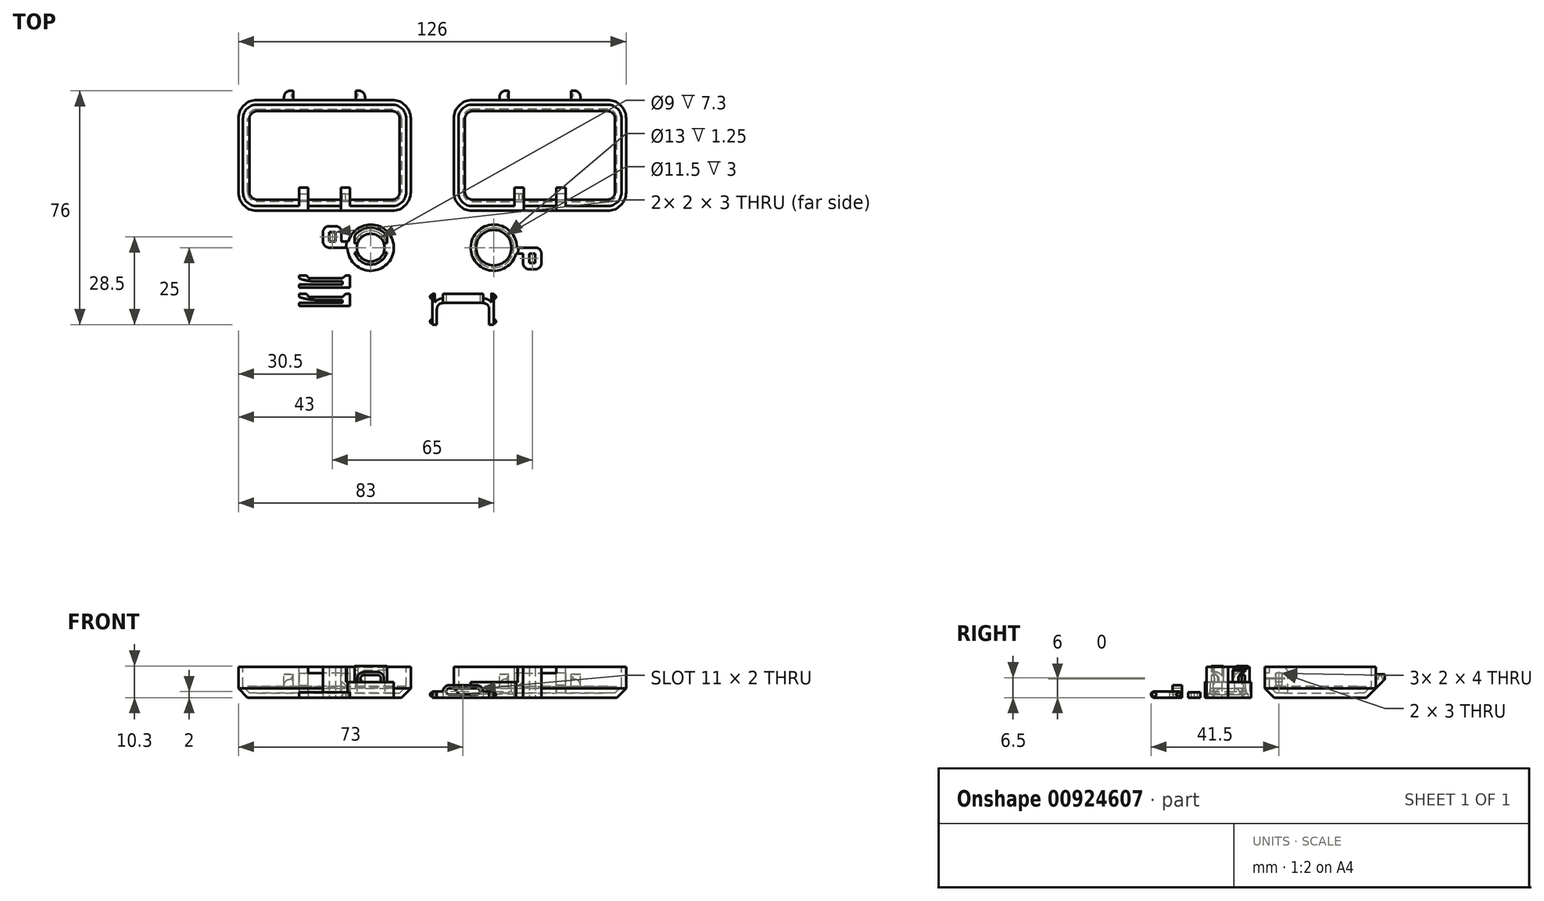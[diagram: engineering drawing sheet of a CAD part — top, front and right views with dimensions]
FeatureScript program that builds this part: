
annotation { "Feature Type Name" : "Feature", "Feature Type Description" : "" }
export const myFeature = defineFeature(function(context is Context, id is Id, definition is map)
    precondition{}
    {
        {
            var Q0;
            Q0=qCreatedBy(makeId("Top.planeOp"),FACE);
            var sketch = newSketch(context, id + "F0", { "sketchPlane" : qUnion([Q0])});
            skCircle(sketch, "E0", {"center": v(-20, 0) * mm, "radius": 7.5 * mm});
            skLineSegment(sketch, "E1", {"start": v(0, 7) * mm, "end": v(0, 0) * mm, "construction": true});
            skLineSegment(sketch, "E2", {"start": v(-27.5, 0) * mm, "end": v(-33.5, 0) * mm});
            skLineSegment(sketch, "E3", {"start": v(-35.5, 2) * mm, "end": v(-35.5, 5) * mm});
            skLineSegment(sketch, "E4", {"start": v(-33.5, 7) * mm, "end": v(-31.5, 7) * mm});
            skLineSegment(sketch, "E5", {"start": v(-29.5, 5) * mm, "end": v(-29.5, 2) * mm});
            skLineSegment(sketch, "E6", {"start": v(-29.5, 2) * mm, "end": v(-27.23, 2) * mm});
            skLineSegment(sketch, "E7.bottom", {"start": v(-33.5, 5) * mm, "end": v(-31.5, 5) * mm});
            skLineSegment(sketch, "E7.top", {"start": v(-33.5, 2) * mm, "end": v(-31.5, 2) * mm});
            skLineSegment(sketch, "E7.left", {"start": v(-33.5, 5) * mm, "end": v(-33.5, 2) * mm});
            skLineSegment(sketch, "E7.right", {"start": v(-31.5, 5) * mm, "end": v(-31.5, 2) * mm});
            skCircle(sketch, "E8", {"center": v(-20, 0) * mm, "radius": 4.5 * mm});
            skPoint(sketch, "E9.visualSharp", {"position": v(-35.5, 0) * mm});
            skArc(sketch, "E9.filletArc", {"start": v(-35.5, 2) * mm, "mid": v(-34.91, 0.59) * mm, "end": v(-33.5, 0) * mm});
            skPoint(sketch, "E10.visualSharp", {"position": v(-35.5, 7) * mm});
            skArc(sketch, "E10.filletArc", {"start": v(-33.5, 7) * mm, "mid": v(-34.91, 6.41) * mm, "end": v(-35.5, 5) * mm});
            skPoint(sketch, "E11.visualSharp", {"position": v(-29.5, 7) * mm});
            skArc(sketch, "E11.filletArc", {"start": v(-29.5, 5) * mm, "mid": v(-30.09, 6.41) * mm, "end": v(-31.5, 7) * mm});
            skCircle(sketch, "E12.MirrorC", {"center": v(20, 0) * mm, "radius": 7.5 * mm});
            skLineSegment(sketch, "E13.MirrorCS", {"start": v(27.5, 0) * mm, "end": v(33.5, 0) * mm});
            skLineSegment(sketch, "E14.MirrorCS", {"start": v(29.5, 2) * mm, "end": v(27.23, 2) * mm, "construction": true});
            skLineSegment(sketch, "E15.MirrorCS", {"start": v(29.5, 5) * mm, "end": v(29.5, 2) * mm, "construction": true});
            skArc(sketch, "E16.MirrorCS", {"start": v(29.5, 5) * mm, "mid": v(30.09, 6.41) * mm, "end": v(31.5, 7) * mm, "construction": true});
            skLineSegment(sketch, "E17.MirrorCS", {"start": v(33.5, 7) * mm, "end": v(31.5, 7) * mm, "construction": true});
            skArc(sketch, "E18.MirrorCS", {"start": v(33.5, 7) * mm, "mid": v(34.91, 6.41) * mm, "end": v(35.5, 5) * mm, "construction": true});
            skLineSegment(sketch, "E19.MirrorCS", {"start": v(35.5, 2) * mm, "end": v(35.5, 5) * mm, "construction": true});
            skArc(sketch, "E20.MirrorCS", {"start": v(35.5, 2) * mm, "mid": v(34.91, 0.59) * mm, "end": v(33.5, 0) * mm, "construction": true});
            skLineSegment(sketch, "E21.MirrorCS", {"start": v(33.5, 5) * mm, "end": v(33.5, 2) * mm, "construction": true});
            skLineSegment(sketch, "E22.MirrorCS", {"start": v(33.5, 5) * mm, "end": v(31.5, 5) * mm, "construction": true});
            skLineSegment(sketch, "E23.MirrorCS", {"start": v(31.5, 5) * mm, "end": v(31.5, 2) * mm, "construction": true});
            skLineSegment(sketch, "E24.MirrorCS", {"start": v(33.5, 2) * mm, "end": v(31.5, 2) * mm, "construction": true});
            skCircle(sketch, "E25", {"center": v(20, 0) * mm, "radius": 6.5 * mm});
            skLineSegment(sketch, "E26.MirrorCS", {"start": v(29.5, -2) * mm, "end": v(27.23, -2) * mm});
            skLineSegment(sketch, "E27.MirrorCS", {"start": v(29.5, -5) * mm, "end": v(29.5, -2) * mm});
            skArc(sketch, "E28.MirrorCS", {"start": v(29.5, -5) * mm, "mid": v(30.09, -6.41) * mm, "end": v(31.5, -7) * mm});
            skLineSegment(sketch, "E29.MirrorCS", {"start": v(33.5, -7) * mm, "end": v(31.5, -7) * mm});
            skArc(sketch, "E30.MirrorCS", {"start": v(33.5, -7) * mm, "mid": v(34.91, -6.41) * mm, "end": v(35.5, -5) * mm});
            skLineSegment(sketch, "E31.MirrorCS", {"start": v(35.5, -2) * mm, "end": v(35.5, -5) * mm});
            skArc(sketch, "E32.MirrorCS", {"start": v(35.5, -2) * mm, "mid": v(34.91, -0.59) * mm, "end": v(33.5, 0) * mm});
            skLineSegment(sketch, "E33.MirrorCS", {"start": v(33.5, -5) * mm, "end": v(33.5, -2) * mm});
            skLineSegment(sketch, "E34.MirrorCS", {"start": v(33.5, -2) * mm, "end": v(31.5, -2) * mm});
            skLineSegment(sketch, "E35.MirrorCS", {"start": v(31.5, -5) * mm, "end": v(31.5, -2) * mm});
            skLineSegment(sketch, "E36.MirrorCS", {"start": v(33.5, -5) * mm, "end": v(31.5, -5) * mm});
            skSolve(sketch);
        }
        {
            var Q0;
            Q0=makeQuery(id+"F0.imprint","IMPRINT",FACE,{"disambiguationData":[TD([[makeQuery(id+"F0.imprint","IMPRINT",EDGE,{"derivedFrom":sQuery(id+"F0.wireOp",EDGE,"E8")}),-1.0]])]});
            var Q1;
            Q1=makeQuery(id+"F0.imprint","IMPRINT",FACE,{"disambiguationData":[TD([[makeQuery(id+"F0.imprint","IMPRINT",EDGE,{"derivedFrom":sQuery(id+"F0.wireOp",EDGE,"E25")}),-1.0]])]});
            extrude(context, id + "F1", {"entities" : qUnion([Q0, Q1]), "depth" : 5 * mm, "offsetDistance" : 25 * mm});
        }
        {
            var Q0;
            Q0=makeQuery(id+"F1.opExtrude","CAP_FACE",FACE,{"disambiguationData":[OSD([sQuery(id+"F0.wireOp",EDGE,"E0"),sQuery(id+"F0.wireOp",EDGE,"E2"),sQuery(id+"F0.wireOp",EDGE,"E3"),sQuery(id+"F0.wireOp",EDGE,"E4"),sQuery(id+"F0.wireOp",EDGE,"E5"),sQuery(id+"F0.wireOp",EDGE,"E6"),sQuery(id+"F0.wireOp",EDGE,"E7.bottom"),sQuery(id+"F0.wireOp",EDGE,"E7.top"),sQuery(id+"F0.wireOp",EDGE,"E7.left"),sQuery(id+"F0.wireOp",EDGE,"E7.right"),sQuery(id+"F0.wireOp",EDGE,"E8"),sQuery(id+"F0.wireOp",EDGE,"E9.filletArc"),sQuery(id+"F0.wireOp",EDGE,"E10.filletArc"),sQuery(id+"F0.wireOp",EDGE,"E11.filletArc")])],"isStart":false});
            var sketch = newSketch(context, id + "F2", { "sketchPlane" : qUnion([Q0])});
            skArc(sketch, "E37.0", {"start": v(-24.24, -1.5) * mm, "mid": v(-20, -4.5) * mm, "end": v(-15.76, -1.5) * mm});
            skArc(sketch, "E38", {"start": v(-25.3, -1.5) * mm, "mid": v(-20, -5.5) * mm, "end": v(-14.7, -1.5) * mm});
            skLineSegment(sketch, "E39.0", {"start": v(0, 7) * mm, "end": v(0, 0) * mm, "construction": true});
            skLineSegment(sketch, "E40.bottom", {"start": v(-10, -1.5) * mm, "end": v(-14.7, -1.5) * mm, "construction": true});
            skLineSegment(sketch, "E40.top", {"start": v(-10, 1.5) * mm, "end": v(-14.7, 1.5) * mm, "construction": true});
            skLineSegment(sketch, "E40.left", {"start": v(-10, -1.5) * mm, "end": v(-10, 1.5) * mm, "construction": true});
            skLineSegment(sketch, "E40.right", {"start": v(-30, -1.5) * mm, "end": v(-30, 1.5) * mm, "construction": true});
            skArc(sketch, "E41.trimOffspring", {"start": v(-15.76, 1.5) * mm, "mid": v(-20, 4.5) * mm, "end": v(-24.24, 1.5) * mm});
            skArc(sketch, "E42.trimOffspring", {"start": v(-14.7, 1.5) * mm, "mid": v(-20, 5.5) * mm, "end": v(-25.3, 1.5) * mm});
            skLineSegment(sketch, "E43", {"start": v(-25.3, 1.5) * mm, "end": v(-30, 1.5) * mm, "construction": true});
            skLineSegment(sketch, "E44", {"start": v(-24.24, 1.5) * mm, "end": v(-25.3, 1.5) * mm});
            skLineSegment(sketch, "E45", {"start": v(-24.24, -1.5) * mm, "end": v(-25.3, -1.5) * mm});
            skLineSegment(sketch, "E46", {"start": v(-25.3, -1.5) * mm, "end": v(-30, -1.5) * mm, "construction": true});
            skLineSegment(sketch, "E47", {"start": v(-15.76, -1.5) * mm, "end": v(-24.24, -1.5) * mm, "construction": true});
            skLineSegment(sketch, "E48", {"start": v(-14.7, -1.5) * mm, "end": v(-15.76, -1.5) * mm});
            skLineSegment(sketch, "E49", {"start": v(-15.76, 1.5) * mm, "end": v(-24.24, 1.5) * mm, "construction": true});
            skLineSegment(sketch, "E50", {"start": v(-14.7, 1.5) * mm, "end": v(-15.76, 1.5) * mm});
            skCircle(sketch, "E51.0", {"center": v(20, 0) * mm, "radius": 6.5 * mm});
            skCircle(sketch, "E52", {"center": v(20, 0) * mm, "radius": 5.75 * mm});
            skCircle(sketch, "E53", {"center": v(-20, 0) * mm, "radius": 8 * mm});
            skCircle(sketch, "E54.0", {"center": v(-20, 0) * mm, "radius": 7.5 * mm, "construction": true});
            skCircle(sketch, "E55.MirrorC", {"center": v(20, 0) * mm, "radius": 8 * mm});
            skSolve(sketch);
        }
        {
            var Q0;
            Q0=makeQuery(id+"F2.imprint","IMPRINT",FACE,{"disambiguationData":[TD([[makeQuery(id+"F2.imprint","IMPRINT",EDGE,{"derivedFrom":sQuery(id+"F2.wireOp",EDGE,"E37.0")}),-1.0]])]});
            var Q1;
            Q1=makeQuery(id+"F2.imprint","IMPRINT",FACE,{"disambiguationData":[TD([[makeQuery(id+"F2.imprint","IMPRINT",EDGE,{"derivedFrom":sQuery(id+"F2.wireOp",EDGE,"E41.trimOffspring")}),-1.0]])]});
            extrude(context, id + "F3", {"entities" : qUnion([Q0, Q1]), "operationType" : NewBodyOperationType.ADD, "depth" : 5.3 * mm, "offsetDistance" : 25 * mm});
        }
        {
            var Q0;
            Q0=makeQuery(id+"F2.imprint","IMPRINT",FACE,{"disambiguationData":[TD([[makeQuery(id+"F2.imprint","IMPRINT",EDGE,{"derivedFrom":sQuery(id+"F2.wireOp",EDGE,"E51.0")}),1.0]])]});
            extrude(context, id + "F4", {"entities" : qUnion([Q0]), "operationType" : NewBodyOperationType.ADD, "oppositeDirection" : true, "depth" : 4 * mm, "offsetDistance" : 25 * mm});
        }
        {
            var Q0;
            {var subQ1=sQuery(id+"F0.wireOp",EDGE,"E2");Q0=makeQuery(id+"F0.imprint","IMPRINT",FACE,{"disambiguationData":[TD([[makeQuery(id+"F0.imprint","IMPRINT",EDGE,{"derivedFrom":subQ1}),-1.0]])]});}
            var Q1;
            {var subQ0=sQuery(id+"F0.wireOp",EDGE,"E13.MirrorCS");Q1=makeQuery(id+"F0.imprint","IMPRINT",FACE,{"disambiguationData":[TD([[makeQuery(id+"F0.imprint","IMPRINT",EDGE,{"derivedFrom":subQ0}),1.0]])]});}
            var Q2;
            {var subQ0=sQuery(id+"F0.wireOp",EDGE,"E13.MirrorCS");Q2=makeQuery(id+"F0.imprint","IMPRINT",FACE,{"disambiguationData":[TD([[makeQuery(id+"F0.imprint","IMPRINT",EDGE,{"derivedFrom":subQ0}),-1.0]])]});}
            extrude(context, id + "F5", {"entities" : qUnion([Q0, Q1, Q2]), "operationType" : NewBodyOperationType.ADD, "depth" : 10 * mm, "offsetDistance" : 25 * mm});
        }
        {
            var Q0;
            Q0=makeQuery(id+"F3.opExtrude","CAP_FACE",FACE,{"disambiguationData":[OSD([sQuery(id+"F2.wireOp",EDGE,"E41.trimOffspring"),sQuery(id+"F2.wireOp",EDGE,"E42.trimOffspring"),sQuery(id+"F2.wireOp",EDGE,"E44"),sQuery(id+"F2.wireOp",EDGE,"E50")])],"isStart":false});
            var sketch = newSketch(context, id + "F6", { "sketchPlane" : qUnion([Q0])});
            skArc(sketch, "E56.0", {"start": v(-14.7, 1.5) * mm, "mid": v(-20, 5.5) * mm, "end": v(-25.3, 1.5) * mm});
            skArc(sketch, "E57.0", {"start": v(-13.68, 1.5) * mm, "mid": v(-20, 6.5) * mm, "end": v(-26.32, 1.5) * mm});
            skLineSegment(sketch, "E58", {"start": v(-25.3, 1.5) * mm, "end": v(-26.32, 1.5) * mm});
            skLineSegment(sketch, "E59", {"start": v(-14.7, 1.5) * mm, "end": v(-13.68, 1.5) * mm});
            skLineSegment(sketch, "E60", {"start": v(-20, 0) * mm, "end": v(0, 0) * mm, "construction": true});
            skArc(sketch, "E61.MirrorCS", {"start": v(-14.7, -1.5) * mm, "mid": v(-20, -5.5) * mm, "end": v(-25.3, -1.5) * mm});
            skArc(sketch, "E62.MirrorCS", {"start": v(-13.68, -1.5) * mm, "mid": v(-20, -6.5) * mm, "end": v(-26.32, -1.5) * mm});
            skLineSegment(sketch, "E63.MirrorCS", {"start": v(-25.3, -1.5) * mm, "end": v(-26.32, -1.5) * mm});
            skLineSegment(sketch, "E64.MirrorCS", {"start": v(-14.7, -1.5) * mm, "end": v(-13.68, -1.5) * mm});
            skSolve(sketch);
        }
        {
            var Q0;
            Q0=makeQuery(id+"F6.imprint","IMPRINT",FACE,{"disambiguationData":[TD([[makeQuery(id+"F6.imprint","IMPRINT",EDGE,{"derivedFrom":sQuery(id+"F6.wireOp",EDGE,"E61.MirrorCS")}),1.0]])]});
            var Q1;
            Q1=makeQuery(id+"F6.imprint","IMPRINT",FACE,{"disambiguationData":[TD([[makeQuery(id+"F6.imprint","IMPRINT",EDGE,{"derivedFrom":sQuery(id+"F6.wireOp",EDGE,"E56.0")}),-1.0]])]});
            extrude(context, id + "F7", {"entities" : qUnion([Q0, Q1]), "operationType" : NewBodyOperationType.ADD, "oppositeDirection" : true, "depth" : 1.5 * mm, "offsetDistance" : 25 * mm});
        }
        {
            var Q0;
            Q0=makeQuery(id+"F4.opExtrude","CAP_EDGE",EDGE,{"disambiguationData":[OSD([sQuery(id+"F2.wireOp",EDGE,"E52")])],"isStart":false});
            var Q1;
            Q1=makeQuery(id+"F7.opExtrude","CAP_EDGE",EDGE,{"disambiguationData":[OSD([sQuery(id+"F6.wireOp",EDGE,"E62.MirrorCS")])],"isStart":false});
            var Q2;
            Q2=makeQuery(id+"F7.opExtrude","CAP_EDGE",EDGE,{"disambiguationData":[OSD([sQuery(id+"F6.wireOp",EDGE,"E57.0")])],"isStart":false});
            chamfer(context, id + "F8", {"entities" : qUnion([Q0, Q1, Q2]), "width" : 1 * mm, "tangentPropagation" : true});
        }
        {
            var Q0;
            Q0=makeQuery(id+"F2.imprint","IMPRINT",FACE,{"disambiguationData":[TD([[makeQuery(id+"F2.imprint","IMPRINT",EDGE,{"derivedFrom":sQuery(id+"F2.wireOp",EDGE,"E53")}),1.0]])]});
            var Q1;
            Q1=makeQuery(id+"F2.imprint","IMPRINT",FACE,{"disambiguationData":[TD([[makeQuery(id+"F2.imprint","IMPRINT",EDGE,{"derivedFrom":sQuery(id+"F2.wireOp",EDGE,"E51.0")}),-1.0]])]});
            extrude(context, id + "F9", {"entities" : qUnion([Q0, Q1]), "operationType" : NewBodyOperationType.REMOVE, "endBound" : BoundingType.THROUGH_ALL, "depth" : 25 * mm, "offsetDistance" : 25 * mm});
        }
        {
            var Q0;
            Q0=qCreatedBy(makeId("Front.planeOp"),FACE);
            var sketch = newSketch(context, id + "F10", { "sketchPlane" : qUnion([Q0])});
            skLineSegment(sketch, "E65.0.0", {"start": v(-25.3, 5) * mm, "end": v(-14.7, 5) * mm, "construction": true});
            skLineSegment(sketch, "E65.0.1", {"start": v(-14.7, 5) * mm, "end": v(-14.7, 8.8) * mm, "construction": true});
            skLineSegment(sketch, "E65.0.2", {"start": v(-14.7, 8.8) * mm, "end": v(-25.3, 8.8) * mm, "construction": true});
            skLineSegment(sketch, "E65.0.3", {"start": v(-25.3, 8.8) * mm, "end": v(-25.3, 5) * mm, "construction": true});
            skLineSegment(sketch, "E66.bottom", {"start": v(-24.3, 5) * mm, "end": v(-15.7, 5) * mm});
            skLineSegment(sketch, "E66.top", {"start": v(-22.3, 8.3) * mm, "end": v(-17.7, 8.3) * mm});
            skLineSegment(sketch, "E66.left", {"start": v(-24.3, 5) * mm, "end": v(-24.3, 6.3) * mm});
            skLineSegment(sketch, "E66.right", {"start": v(-15.7, 5) * mm, "end": v(-15.7, 6.3) * mm});
            skLineSegment(sketch, "E67.bottom", {"start": v(-23.3, 5) * mm, "end": v(-16.7, 5) * mm});
            skLineSegment(sketch, "E67.top", {"start": v(-22.3, 7.3) * mm, "end": v(-17.7, 7.3) * mm});
            skLineSegment(sketch, "E67.left", {"start": v(-23.3, 5) * mm, "end": v(-23.3, 6.3) * mm});
            skLineSegment(sketch, "E67.right", {"start": v(-16.7, 5) * mm, "end": v(-16.7, 6.3) * mm});
            skPoint(sketch, "E68.visualSharp", {"position": v(-23.3, 7.3) * mm});
            skArc(sketch, "E68.filletArc", {"start": v(-22.3, 7.3) * mm, "mid": v(-23, 7) * mm, "end": v(-23.3, 6.3) * mm});
            skPoint(sketch, "E69.visualSharp", {"position": v(-16.7, 7.3) * mm});
            skArc(sketch, "E69.filletArc", {"start": v(-16.7, 6.3) * mm, "mid": v(-17, 7) * mm, "end": v(-17.7, 7.3) * mm});
            skPoint(sketch, "E70.visualSharp", {"position": v(-15.7, 8.3) * mm});
            skArc(sketch, "E70.filletArc", {"start": v(-15.7, 6.3) * mm, "mid": v(-16.3, 7.71) * mm, "end": v(-17.7, 8.3) * mm});
            skPoint(sketch, "E71.visualSharp", {"position": v(-24.3, 8.3) * mm});
            skArc(sketch, "E71.filletArc", {"start": v(-22.3, 8.3) * mm, "mid": v(-23.7, 7.71) * mm, "end": v(-24.3, 6.3) * mm});
            skLineSegment(sketch, "E72.bottom", {"start": v(-25.3, 5) * mm, "end": v(-27.3, 5) * mm});
            skLineSegment(sketch, "E72.top", {"start": v(-25.3, 11) * mm, "end": v(-27.3, 11) * mm});
            skLineSegment(sketch, "E72.left", {"start": v(-25.3, 5) * mm, "end": v(-25.3, 11) * mm});
            skLineSegment(sketch, "E72.right", {"start": v(-27.3, 5) * mm, "end": v(-27.3, 11) * mm});
            skLineSegment(sketch, "E73.bottom", {"start": v(-14.7, 5) * mm, "end": v(-12.7, 5) * mm});
            skLineSegment(sketch, "E73.top", {"start": v(-14.7, 11) * mm, "end": v(-12.7, 11) * mm});
            skLineSegment(sketch, "E73.left", {"start": v(-14.7, 5) * mm, "end": v(-14.7, 11) * mm});
            skLineSegment(sketch, "E73.right", {"start": v(-12.7, 5) * mm, "end": v(-12.7, 11) * mm});
            skSolve(sketch);
        }
        {
            var Q0;
            Q0=makeQuery(id+"F10.imprint","IMPRINT",FACE,{"disambiguationData":[TD([[makeQuery(id+"F10.imprint","IMPRINT",EDGE,{"derivedFrom":sQuery(id+"F10.wireOp",EDGE,"E66.top")}),-1.0]])]});
            var Q1;
            Q1=makeQuery(id+"F10.imprint","IMPRINT",FACE,{"disambiguationData":[TD([[makeQuery(id+"F10.imprint","IMPRINT",EDGE,{"derivedFrom":sQuery(id+"F10.wireOp",EDGE,"E72.bottom")}),-1.0]])]});
            var Q2;
            Q2=makeQuery(id+"F10.imprint","IMPRINT",FACE,{"disambiguationData":[TD([[makeQuery(id+"F10.imprint","IMPRINT",EDGE,{"derivedFrom":sQuery(id+"F10.wireOp",EDGE,"E73.bottom")}),1.0]])]});
            extrude(context, id + "F11", {"entities" : qUnion([Q0, Q1, Q2]), "operationType" : NewBodyOperationType.REMOVE, "endBound" : BoundingType.THROUGH_ALL, "oppositeDirection" : true, "depth" : 25 * mm, "offsetDistance" : 25 * mm, "hasSecondDirection" : true, "secondDirectionBound" : SecondDirectionBoundingType.THROUGH_ALL, "secondDirectionOppositeDirection" : false, "secondDirectionDepth" : 25 * mm});
        }
        {
            var Q0;
            Q0=qCreatedBy(makeId("Top.planeOp"),FACE);
            var sketch = newSketch(context, id + "F12", { "sketchPlane" : qUnion([Q0])});
            skLineSegment(sketch, "E74.bottom", {"start": v(-13, 15) * mm, "end": v(-57, 15) * mm});
            skLineSegment(sketch, "E74.top", {"start": v(-13, 45) * mm, "end": v(-57, 45) * mm});
            skLineSegment(sketch, "E74.left", {"start": v(-10, 18) * mm, "end": v(-10, 42) * mm});
            skLineSegment(sketch, "E74.right", {"start": v(-60, 18) * mm, "end": v(-60, 42) * mm});
            skPoint(sketch, "E74.middle", {"position": v(-35, 30) * mm});
            skPoint(sketch, "E75.visualSharp", {"position": v(-60, 45) * mm});
            skArc(sketch, "E75.filletArc", {"start": v(-57, 45) * mm, "mid": v(-59.12, 44.12) * mm, "end": v(-60, 42) * mm});
            skPoint(sketch, "E76.visualSharp", {"position": v(-10, 45) * mm});
            skArc(sketch, "E76.filletArc", {"start": v(-10, 42) * mm, "mid": v(-10.88, 44.12) * mm, "end": v(-13, 45) * mm});
            skPoint(sketch, "E77.visualSharp", {"position": v(-10, 15) * mm});
            skArc(sketch, "E77.filletArc", {"start": v(-13, 15) * mm, "mid": v(-10.88, 15.88) * mm, "end": v(-10, 18) * mm});
            skPoint(sketch, "E78.visualSharp", {"position": v(-60, 15) * mm});
            skArc(sketch, "E78.filletArc", {"start": v(-60, 18) * mm, "mid": v(-59.12, 15.88) * mm, "end": v(-57, 15) * mm});
            skSolve(sketch);
        }
        {
            var Q0;
            Q0=makeQuery(id+"F12.imprint","IMPRINT",FACE,{"disambiguationData":[TD([[makeQuery(id+"F12.imprint","IMPRINT",EDGE,{"derivedFrom":sQuery(id+"F12.wireOp",EDGE,"E74.bottom")}),-1.0]])]});
            extrude(context, id + "F13", {"entities" : qUnion([Q0]), "depth" : 3 * mm, "offsetDistance" : 25 * mm, "hasDraft" : true, "draftAngle" : 45 * degree});
        }
        {
            var Q0;
            Q0=makeQuery(id+"F13.opExtrude","CAP_FACE",FACE,{"disambiguationData":[OSD([sQuery(id+"F12.wireOp",EDGE,"E74.bottom"),sQuery(id+"F12.wireOp",EDGE,"E74.top"),sQuery(id+"F12.wireOp",EDGE,"E74.left"),sQuery(id+"F12.wireOp",EDGE,"E74.right"),sQuery(id+"F12.wireOp",EDGE,"E75.filletArc"),sQuery(id+"F12.wireOp",EDGE,"E76.filletArc"),sQuery(id+"F12.wireOp",EDGE,"E77.filletArc"),sQuery(id+"F12.wireOp",EDGE,"E78.filletArc")])],"isStart":false});
            extrude(context, id + "F14", {"entities" : qUnion([Q0]), "operationType" : NewBodyOperationType.ADD, "depth" : 7 * mm, "offsetDistance" : 25 * mm});
        }
        {
            var Q0;
            Q0=makeQuery(id+"F14.opExtrude","CAP_FACE",FACE,{"disambiguationData":[OSD([sQuery(id+"F12.wireOp",EDGE,"E74.bottom"),sQuery(id+"F12.wireOp",EDGE,"E74.top"),sQuery(id+"F12.wireOp",EDGE,"E74.left"),sQuery(id+"F12.wireOp",EDGE,"E74.right"),sQuery(id+"F12.wireOp",EDGE,"E75.filletArc"),sQuery(id+"F12.wireOp",EDGE,"E76.filletArc"),sQuery(id+"F12.wireOp",EDGE,"E77.filletArc"),sQuery(id+"F12.wireOp",EDGE,"E78.filletArc")])],"isStart":false});
            shell(context, id + "F15", {"entities" : qUnion([Q0]), "thickness" : 1.5 * mm});
        }
        {
            var Q0;
            Q0=makeQuery(id+"F14.opExtrude","CAP_FACE",FACE,{"disambiguationData":[OSD([sQuery(id+"F12.wireOp",EDGE,"E74.bottom"),sQuery(id+"F12.wireOp",EDGE,"E74.top"),sQuery(id+"F12.wireOp",EDGE,"E74.left"),sQuery(id+"F12.wireOp",EDGE,"E74.right"),sQuery(id+"F12.wireOp",EDGE,"E75.filletArc"),sQuery(id+"F12.wireOp",EDGE,"E76.filletArc"),sQuery(id+"F12.wireOp",EDGE,"E77.filletArc"),sQuery(id+"F12.wireOp",EDGE,"E78.filletArc")])],"isStart":false});
            var sketch = newSketch(context, id + "F16", { "sketchPlane" : qUnion([Q0])});
            skLineSegment(sketch, "E79.0", {"start": v(-13, 13.5) * mm, "end": v(-57, 13.5) * mm, "construction": true});
            skLineSegment(sketch, "E80.0", {"start": v(-13, 12) * mm, "end": v(-57, 12) * mm, "construction": true});
            skLineSegment(sketch, "E81.bottom", {"start": v(-40.3, 13.5) * mm, "end": v(-29.7, 13.5) * mm});
            skLineSegment(sketch, "E81.top", {"start": v(-40.3, 12) * mm, "end": v(-29.7, 12) * mm});
            skLineSegment(sketch, "E81.left", {"start": v(-40.3, 13.5) * mm, "end": v(-40.3, 12) * mm});
            skLineSegment(sketch, "E81.right", {"start": v(-29.7, 13.5) * mm, "end": v(-29.7, 12) * mm});
            skLineSegment(sketch, "E82", {"start": v(-35, 13.5) * mm, "end": v(-35, 12) * mm, "construction": true});
            skLineSegment(sketch, "E83.bottom", {"start": v(-29.7, 13.5) * mm, "end": v(-26.7, 13.5) * mm});
            skLineSegment(sketch, "E83.top", {"start": v(-29.7, 19.5) * mm, "end": v(-26.7, 19.5) * mm});
            skLineSegment(sketch, "E83.left", {"start": v(-29.7, 13.5) * mm, "end": v(-29.7, 19.5) * mm});
            skLineSegment(sketch, "E83.right", {"start": v(-26.7, 13.5) * mm, "end": v(-26.7, 19.5) * mm});
            skLineSegment(sketch, "E84.bottom", {"start": v(-40.3, 13.5) * mm, "end": v(-43.3, 13.5) * mm});
            skLineSegment(sketch, "E84.top", {"start": v(-40.3, 19.5) * mm, "end": v(-43.3, 19.5) * mm});
            skLineSegment(sketch, "E84.left", {"start": v(-40.3, 13.5) * mm, "end": v(-40.3, 19.5) * mm});
            skLineSegment(sketch, "E84.right", {"start": v(-43.3, 13.5) * mm, "end": v(-43.3, 19.5) * mm});
            skLineSegment(sketch, "E85.0", {"start": v(-13, 48) * mm, "end": v(-57, 48) * mm, "construction": true});
            skLineSegment(sketch, "E86.bottom", {"start": v(-48.15, 48) * mm, "end": v(-45.15, 48) * mm});
            skLineSegment(sketch, "E86.top", {"start": v(-46.15, 51) * mm, "end": v(-45.15, 51) * mm});
            skLineSegment(sketch, "E86.left", {"start": v(-48.15, 48) * mm, "end": v(-48.15, 49) * mm});
            skLineSegment(sketch, "E86.right", {"start": v(-45.15, 48) * mm, "end": v(-45.15, 51) * mm});
            skLineSegment(sketch, "E87.bottom", {"start": v(-24.85, 48) * mm, "end": v(-21.85, 48) * mm});
            skLineSegment(sketch, "E87.top", {"start": v(-24.85, 51) * mm, "end": v(-23.85, 51) * mm});
            skLineSegment(sketch, "E87.left", {"start": v(-24.85, 48) * mm, "end": v(-24.85, 51) * mm});
            skLineSegment(sketch, "E87.right", {"start": v(-21.85, 48) * mm, "end": v(-21.85, 49) * mm});
            skLineSegment(sketch, "E88", {"start": v(-45.15, 51) * mm, "end": v(-35, 51) * mm, "construction": true});
            skLineSegment(sketch, "E89", {"start": v(-35, 51) * mm, "end": v(-35, 48) * mm, "construction": true});
            skLineSegment(sketch, "E90", {"start": v(-35, 51) * mm, "end": v(-24.85, 51) * mm, "construction": true});
            skPoint(sketch, "E91.visualSharp", {"position": v(-48.15, 51) * mm});
            skArc(sketch, "E91.filletArc", {"start": v(-46.15, 51) * mm, "mid": v(-47.56, 50.41) * mm, "end": v(-48.15, 49) * mm});
            skPoint(sketch, "E92.visualSharp", {"position": v(-21.85, 51) * mm});
            skArc(sketch, "E92.filletArc", {"start": v(-21.85, 49) * mm, "mid": v(-22.44, 50.41) * mm, "end": v(-23.85, 51) * mm});
            skSolve(sketch);
        }
        {
            var Q0;
            Q0=makeQuery(id+"F16.imprint","IMPRINT",FACE,{"disambiguationData":[TD([[makeQuery(id+"F16.imprint","IMPRINT",EDGE,{"derivedFrom":sQuery(id+"F16.wireOp",EDGE,"E81.bottom")}),1.0]])]});
            extrude(context, id + "F17", {"entities" : qUnion([Q0]), "operationType" : NewBodyOperationType.REMOVE, "oppositeDirection" : true, "depth" : 2 * mm, "offsetDistance" : 25 * mm});
        }
        {
            var Q0;
            Q0=makeQuery(id+"F16.imprint","IMPRINT",FACE,{"disambiguationData":[TD([[makeQuery(id+"F16.imprint","IMPRINT",EDGE,{"derivedFrom":sQuery(id+"F16.wireOp",EDGE,"E83.bottom")}),-1.0]])]});
            var Q1;
            Q1=makeQuery(id+"F16.imprint","IMPRINT",FACE,{"disambiguationData":[TD([[makeQuery(id+"F16.imprint","IMPRINT",EDGE,{"derivedFrom":sQuery(id+"F16.wireOp",EDGE,"E84.bottom")}),-1.0]])]});
            extrude(context, id + "F18", {"entities" : qUnion([Q0, Q1]), "operationType" : NewBodyOperationType.ADD, "endBound" : BoundingType.UP_TO_NEXT, "oppositeDirection" : true, "depth" : 7 * mm, "offsetDistance" : 25 * mm});
        }
        {
            var Q0;
            Q0=makeQuery(id+"F18.opExtrude","SWEPT_FACE",FACE,{"disambiguationData":[OSD([sQuery(id+"F16.wireOp",EDGE,"E83.right")])]});
            var sketch = newSketch(context, id + "F19", { "sketchPlane" : qUnion([Q0])});
            skLineSegment(sketch, "E93.bottom", {"start": v(15.5, 8) * mm, "end": v(17.5, 8) * mm});
            skLineSegment(sketch, "E93.top", {"start": v(15.5, 4) * mm, "end": v(17.5, 4) * mm});
            skLineSegment(sketch, "E93.left", {"start": v(15.5, 8) * mm, "end": v(15.5, 4) * mm});
            skLineSegment(sketch, "E93.right", {"start": v(17.5, 8) * mm, "end": v(17.5, 4) * mm});
            skLineSegment(sketch, "E94.0", {"start": v(13.5, 3.62) * mm, "end": v(13.5, 10) * mm, "construction": true});
            skLineSegment(sketch, "E95.0", {"start": v(13.5, 10) * mm, "end": v(19.5, 10) * mm, "construction": true});
            skLineSegment(sketch, "E96.0", {"start": v(19.5, 1.5) * mm, "end": v(19.5, 10) * mm, "construction": true});
            skLineSegment(sketch, "E97", {"start": v(17.5, 5) * mm, "end": v(15.5, 5) * mm});
            skSolve(sketch);
        }
        {
            var Q0;
            Q0 = qSketchRegion(id + "F19", true);
            extrude(context, id + "F20", {"entities" : qUnion([Q0]), "operationType" : NewBodyOperationType.REMOVE, "oppositeDirection" : true, "depth" : 20 * mm, "offsetDistance" : 25 * mm});
        }
        {
            var Q0;
            {var subQ0=sQuery(id+"F19.wireOp",EDGE,"E93.top");Q0=makeQuery(id+"F19.imprint","IMPRINT",FACE,{"disambiguationData":[TD([[makeQuery(id+"F19.imprint","IMPRINT",EDGE,{"derivedFrom":subQ0}),1.0]])]});}
            var Q1;
            Q1=makeQuery(id+"F18.boolean.opBoolean","MERGE",FACE,{"derivedFrom":[makeQuery(id+"F17.boolean.opBoolean","COPY",FACE,{"derivedFrom":makeQuery(id+"F17.opExtrude","SWEPT_FACE",FACE,{"disambiguationData":[OSD([sQuery(id+"F16.wireOp",EDGE,"E81.right")])]})}),makeQuery(id+"F18.opExtrude","SWEPT_FACE",FACE,{"disambiguationData":[OSD([sQuery(id+"F16.wireOp",EDGE,"E83.left")])]})]});
            extrude(context, id + "F21", {"entities" : qUnion([Q0]), "operationType" : NewBodyOperationType.ADD, "endBound" : BoundingType.UP_TO_SURFACE, "oppositeDirection" : true, "depth" : 3 * mm, "endBoundEntityFace" : qUnion([Q1]), "offsetDistance" : 25 * mm, "hasSecondDirection" : true, "secondDirectionOppositeDirection" : true, "secondDirectionDepth" : 1.5 * mm});
        }
        {
            var Q0;
            Q0=makeQuery(id+"F21.opExtrude","CAP_EDGE",EDGE,{"disambiguationData":[OSD([sQuery(id+"F19.wireOp",EDGE,"E97")])],"isStart":true});
            chamfer(context, id + "F22", {"entities" : qUnion([Q0]), "width" : 1 * mm, "tangentPropagation" : true});
        }
        {
            var Q0;
            Q0=makeQuery(id+"F16.imprint","IMPRINT",FACE,{"disambiguationData":[TD([[makeQuery(id+"F16.imprint","IMPRINT",EDGE,{"derivedFrom":sQuery(id+"F16.wireOp",EDGE,"E87.bottom")}),-1.0]])]});
            var Q1;
            Q1=makeQuery(id+"F16.imprint","IMPRINT",FACE,{"disambiguationData":[TD([[makeQuery(id+"F16.imprint","IMPRINT",EDGE,{"derivedFrom":sQuery(id+"F16.wireOp",EDGE,"E86.bottom")}),-1.0]])]});
            var Q2;
            Q2=makeQuery(id+"F13.opExtrude","SWEPT_FACE",FACE,{"disambiguationData":[OSD([sQuery(id+"F12.wireOp",EDGE,"E74.top")])]});
            extrude(context, id + "F23", {"entities" : qUnion([Q0, Q1]), "operationType" : NewBodyOperationType.ADD, "endBound" : BoundingType.UP_TO_SURFACE, "oppositeDirection" : true, "depth" : 10 * mm, "endBoundEntityFace" : qUnion([Q2]), "offsetDistance" : 25 * mm, "hasSecondDirection" : true, "secondDirectionOppositeDirection" : true, "secondDirectionDepth" : 2.4 * mm});
        }
        {
            var Q0;
            Q0=makeQuery(id+"F18.opExtrude","CAP_EDGE",EDGE,{"disambiguationData":[OSD([sQuery(id+"F16.wireOp",EDGE,"E83.top")])],"isStart":true});
            var Q1;
            Q1=makeQuery(id+"F18.opExtrude","CAP_EDGE",EDGE,{"disambiguationData":[OSD([sQuery(id+"F16.wireOp",EDGE,"E84.top")])],"isStart":true});
            var Q2;
            Q2=makeQuery(id+"F7.boolean.opBoolean","MERGE",EDGE,{"derivedFrom":[makeQuery(id+"F3.opExtrude","CAP_EDGE",EDGE,{"disambiguationData":[OSD([sQuery(id+"F2.wireOp",EDGE,"E44")])],"isStart":false}),makeQuery(id+"F7.opExtrude","CAP_EDGE",EDGE,{"disambiguationData":[OSD([sQuery(id+"F6.wireOp",EDGE,"E58")])],"isStart":true})]});
            var Q3;
            Q3=makeQuery(id+"F7.boolean.opBoolean","MERGE",EDGE,{"derivedFrom":[makeQuery(id+"F3.opExtrude","CAP_EDGE",EDGE,{"disambiguationData":[OSD([sQuery(id+"F2.wireOp",EDGE,"E45")])],"isStart":false}),makeQuery(id+"F7.opExtrude","CAP_EDGE",EDGE,{"disambiguationData":[OSD([sQuery(id+"F6.wireOp",EDGE,"E63.MirrorCS")])],"isStart":true})]});
            var Q4;
            Q4=makeQuery(id+"F7.boolean.opBoolean","MERGE",EDGE,{"derivedFrom":[makeQuery(id+"F3.opExtrude","CAP_EDGE",EDGE,{"disambiguationData":[OSD([sQuery(id+"F2.wireOp",EDGE,"E50")])],"isStart":false}),makeQuery(id+"F7.opExtrude","CAP_EDGE",EDGE,{"disambiguationData":[OSD([sQuery(id+"F6.wireOp",EDGE,"E59")])],"isStart":true})]});
            var Q5;
            Q5=makeQuery(id+"F7.boolean.opBoolean","MERGE",EDGE,{"derivedFrom":[makeQuery(id+"F3.opExtrude","CAP_EDGE",EDGE,{"disambiguationData":[OSD([sQuery(id+"F2.wireOp",EDGE,"E48")])],"isStart":false}),makeQuery(id+"F7.opExtrude","CAP_EDGE",EDGE,{"disambiguationData":[OSD([sQuery(id+"F6.wireOp",EDGE,"E64.MirrorCS")])],"isStart":true})]});
            fillet(context, id + "F24", {"entities" : qUnion([Q0, Q1, Q2, Q3, Q4, Q5]), "radius" : 2 * mm, "tangentPropagation" : true, "allowEdgeOverflow" : false});
        }
        {
            var Q0;
            Q0=qCreatedBy(makeId("Top.planeOp"),FACE);
            var sketch = newSketch(context, id + "F25", { "sketchPlane" : qUnion([Q0])});
            skLineSegment(sketch, "E98.0", {"start": v(-43.3, 13.5) * mm, "end": v(-43.3, 17.5) * mm, "construction": true});
            skLineSegment(sketch, "E99.0", {"start": v(-26.7, 13.5) * mm, "end": v(-26.7, 17.5) * mm, "construction": true});
            skLineSegment(sketch, "E100.0", {"start": v(-40.3, 17.5) * mm, "end": v(-40.3, 12) * mm, "construction": true});
            skPoint(sketch, "E101.0", {"position": v(0, 0) * mm});
            skLineSegment(sketch, "E102", {"start": v(0, 0) * mm, "end": v(0, -15) * mm, "construction": true});
            skLineSegment(sketch, "E103", {"start": v(0, -15) * mm, "end": v(-43.3, -15) * mm, "construction": true});
            skLineSegment(sketch, "E104", {"start": v(-40.3, -16) * mm, "end": v(-40.3, -16) * mm});
            skLineSegment(sketch, "E105", {"start": v(-40.3, -16) * mm, "end": v(-29.2, -16) * mm});
            skLineSegment(sketch, "E106", {"start": v(-29.2, -16) * mm, "end": v(-28.2, -15) * mm});
            skLineSegment(sketch, "E107", {"start": v(-28.2, -15) * mm, "end": v(-26.7, -15) * mm});
            skLineSegment(sketch, "E108", {"start": v(-26.7, -15) * mm, "end": v(-26.7, -19) * mm});
            skLineSegment(sketch, "E109", {"start": v(-26.7, -19) * mm, "end": v(-43.3, -19) * mm});
            skLineSegment(sketch, "E110", {"start": v(-43.3, -19) * mm, "end": v(-43.3, -18) * mm});
            skLineSegment(sketch, "E111.0", {"start": v(-28.2, 15.5) * mm, "end": v(-28.2, 17.5) * mm, "construction": true});
            skLineSegment(sketch, "E112.0", {"start": v(-29.7, 17.5) * mm, "end": v(-29.7, 12) * mm, "construction": true});
            skLineSegment(sketch, "E113.0", {"start": v(-29.2, 15.5) * mm, "end": v(-29.2, 17.5) * mm, "construction": true});
            skLineSegment(sketch, "E114", {"start": v(-29.2, -17) * mm, "end": v(-37.87, -17) * mm});
            skLineSegment(sketch, "E115", {"start": v(-29.2, -17) * mm, "end": v(-29.2, -18) * mm});
            skLineSegment(sketch, "E116", {"start": v(-29.2, -18) * mm, "end": v(-43.3, -18) * mm});
            skLineSegment(sketch, "E117.trimOffspring", {"start": v(-43.3, -16) * mm, "end": v(-43.3, -15) * mm});
            skLineSegment(sketch, "E118", {"start": v(-43.3, -15) * mm, "end": v(-41.3, -15) * mm});
            skLineSegment(sketch, "E119", {"start": v(-42.6, -16.23) * mm, "end": v(-43.3, -16) * mm});
            skPoint(sketch, "E120.orphan", {"position": v(-43.3, -17) * mm});
            skPoint(sketch, "E121.visualSharp", {"position": v(-40.3, -15) * mm});
            skArc(sketch, "E121.filletArc", {"start": v(-40.3, -16) * mm, "mid": v(-40.6, -15.3) * mm, "end": v(-41.3, -15) * mm});
            skPoint(sketch, "E122.visualSharp", {"position": v(-40.3, -17) * mm});
            skArc(sketch, "E122.filletArc", {"start": v(-42.6, -16.23) * mm, "mid": v(-40.27, -16.8) * mm, "end": v(-37.87, -17) * mm});
            skSolve(sketch);
        }
        {
            var Q0;
            Q0=makeQuery(id+"F25.imprint","IMPRINT",FACE,{"disambiguationData":[TD([[makeQuery(id+"F25.imprint","IMPRINT",EDGE,{"derivedFrom":sQuery(id+"F25.wireOp",EDGE,"E105")}),-1.0]])]});
            extrude(context, id + "F26", {"entities" : qUnion([Q0]), "depth" : 1.75 * mm, "offsetDistance" : 25 * mm});
        }
        {
            var Q0;
            Q0=makeQuery(id+"F26.opExtrude","SWEPT_BODY",BODY,{"disambiguationData":[OSD([sQuery(id+"F25.wireOp",EDGE,"E105"),sQuery(id+"F25.wireOp",EDGE,"E106"),sQuery(id+"F25.wireOp",EDGE,"E107"),sQuery(id+"F25.wireOp",EDGE,"E108"),sQuery(id+"F25.wireOp",EDGE,"E109"),sQuery(id+"F25.wireOp",EDGE,"E110"),sQuery(id+"F25.wireOp",EDGE,"E114"),sQuery(id+"F25.wireOp",EDGE,"E115"),sQuery(id+"F25.wireOp",EDGE,"E116"),sQuery(id+"F25.wireOp",EDGE,"E117.trimOffspring"),sQuery(id+"F25.wireOp",EDGE,"E118"),sQuery(id+"F25.wireOp",EDGE,"E119"),sQuery(id+"F25.wireOp",EDGE,"E121.filletArc"),sQuery(id+"F25.wireOp",EDGE,"E122.filletArc")])]});
            transform(context, id + "F27", {"entities" : qUnion([Q0]), "transformType" : TransformType.TRANSLATION_3D, "dx" : 0 * mm, "dy" : 6 * mm, "dz" : 0 * mm, "makeCopy" : true});
        }
        {
            var Q0;
            Q0=qCreatedBy(makeId("Top.planeOp"),FACE);
            var sketch = newSketch(context, id + "F28", { "sketchPlane" : qUnion([Q0])});
            skLineSegment(sketch, "E123.bottom", {"start": v(0, -25) * mm, "end": v(1.5, -25) * mm});
            skLineSegment(sketch, "E123.top", {"start": v(0, -15) * mm, "end": v(0.8, -15) * mm});
            skLineSegment(sketch, "E123.left", {"start": v(0, -25) * mm, "end": v(0, -15) * mm});
            skLineSegment(sketch, "E123.right", {"start": v(20, -25) * mm, "end": v(20, -15) * mm});
            skLineSegment(sketch, "E124", {"start": v(1.5, -25) * mm, "end": v(1.5, -20) * mm});
            skLineSegment(sketch, "E125", {"start": v(3.5, -18) * mm, "end": v(16.5, -18) * mm});
            skLineSegment(sketch, "E126", {"start": v(18.5, -20) * mm, "end": v(18.5, -25) * mm});
            skLineSegment(sketch, "E127.trimOffspring", {"start": v(18.5, -25) * mm, "end": v(20, -25) * mm});
            skPoint(sketch, "E128.visualSharp", {"position": v(1.5, -18) * mm});
            skArc(sketch, "E128.filletArc", {"start": v(3.5, -18) * mm, "mid": v(2.09, -18.59) * mm, "end": v(1.5, -20) * mm});
            skPoint(sketch, "E129.visualSharp", {"position": v(18.5, -18) * mm});
            skArc(sketch, "E129.filletArc", {"start": v(18.5, -20) * mm, "mid": v(17.91, -18.59) * mm, "end": v(16.5, -18) * mm});
            skPoint(sketch, "E130", {"position": v(0, -20) * mm});
            skPoint(sketch, "E131", {"position": v(0, -24) * mm});
            skArc(sketch, "E132", {"start": v(0.8, -17.77) * mm, "mid": v(2, -16.83) * mm, "end": v(3.5, -16.5) * mm});
            skArc(sketch, "E133", {"start": v(19.2, -17.77) * mm, "mid": v(18, -16.83) * mm, "end": v(16.5, -16.5) * mm});
            skLineSegment(sketch, "E134", {"start": v(0.8, -15) * mm, "end": v(0.8, -17.77) * mm});
            skLineSegment(sketch, "E135", {"start": v(3.5, -16.5) * mm, "end": v(3.5, -15) * mm});
            skLineSegment(sketch, "E136", {"start": v(19.2, -15) * mm, "end": v(19.2, -17.77) * mm});
            skLineSegment(sketch, "E137", {"start": v(16.5, -15) * mm, "end": v(16.5, -16.5) * mm});
            skLineSegment(sketch, "E138.trimOffspring", {"start": v(3.5, -15) * mm, "end": v(16.5, -15) * mm});
            skPoint(sketch, "E139.orphan", {"position": v(3.5, -16.5) * mm});
            skLineSegment(sketch, "E140.trimOffspring", {"start": v(19.2, -15) * mm, "end": v(20, -15) * mm});
            skPoint(sketch, "E141.orphan", {"position": v(20, -20) * mm});
            skPoint(sketch, "E142.orphan", {"position": v(16.5, -16.5) * mm});
            skSolve(sketch);
        }
        {
            var Q0;
            Q0=sQuery(id+"F16.wireOp",EDGE,"E89");
            cPlane(context, id + "F29", {"entities" : qUnion([Q0]), "cplaneType" : CPlaneType.LINE_ANGLE, "offset" : 25 * mm, "angle" : 90 * degree, "width" : 150 * mm, "height" : 150 * mm});
        }
        {
            var Q0;
            Q0=qCreatedBy(id+"F29.planeOp",FACE);
            var sketch = newSketch(context, id + "F30", { "sketchPlane" : qUnion([Q0])});
            skLineSegment(sketch, "E143.0", {"start": v(51, 10) * mm, "end": v(48, 10) * mm, "construction": true});
            skLineSegment(sketch, "E144", {"start": v(48, 10) * mm, "end": v(48, 6.25) * mm, "construction": true});
            skLineSegment(sketch, "E145", {"start": v(48, 6.25) * mm, "end": v(49.5, 6.25) * mm, "construction": true});
            skCircle(sketch, "E146", {"center": v(49.5, 6.25) * mm, "radius": 0.8 * mm});
            skSolve(sketch);
        }
        {
            var Q0;
            Q0=makeQuery(id+"F28.imprint","IMPRINT",FACE,{"disambiguationData":[TD([[makeQuery(id+"F28.imprint","IMPRINT",EDGE,{"derivedFrom":sQuery(id+"F28.wireOp",EDGE,"E123.bottom")}),1.0]])]});
            extrude(context, id + "F31", {"entities" : qUnion([Q0]), "depth" : 2 * mm, "offsetDistance" : 25 * mm});
        }
        {
            var Q0;
            Q0=makeQuery(id+"F31.opExtrude","SWEPT_FACE",FACE,{"disambiguationData":[OSD([sQuery(id+"F28.wireOp",EDGE,"E123.left")])]});
            var sketch = newSketch(context, id + "F32", { "sketchPlane" : qUnion([Q0])});
            skCircle(sketch, "E147", {"center": v(24, 1) * mm, "radius": 0.7 * mm});
            skCircle(sketch, "E148", {"center": v(16, 1) * mm, "radius": 0.7 * mm});
            skSolve(sketch);
        }
        {
            var Q0;
            Q0=makeQuery(id+"F32.imprint","IMPRINT",FACE,{"disambiguationData":[TD([[makeQuery(id+"F32.imprint","IMPRINT",EDGE,{"derivedFrom":sQuery(id+"F32.wireOp",EDGE,"E147")}),1.0]])]});
            var Q1;
            Q1=makeQuery(id+"F32.imprint","IMPRINT",FACE,{"disambiguationData":[TD([[makeQuery(id+"F32.imprint","IMPRINT",EDGE,{"derivedFrom":sQuery(id+"F32.wireOp",EDGE,"E148")}),1.0]])]});
            extrude(context, id + "F33", {"entities" : qUnion([Q0, Q1]), "operationType" : NewBodyOperationType.ADD, "depth" : .7 * mm, "offsetDistance" : 25 * mm});
        }
        {
            var Q0;
            Q0 = qSketchRegion(id + "F32", true);
            extrude(context, id + "F34", {"entities" : qUnion([Q0]), "operationType" : NewBodyOperationType.ADD, "oppositeDirection" : true, "depth" : 20.7 * mm, "offsetDistance" : 25 * mm, "hasSecondDirection" : true, "secondDirectionOppositeDirection" : true, "secondDirectionDepth" : 20 * mm});
        }
        {
            var Q0;
            Q0=makeQuery(id+"F33.opExtrude","CAP_EDGE",EDGE,{"disambiguationData":[OSD([sQuery(id+"F32.wireOp",EDGE,"E147")])],"isStart":false});
            var Q1;
            Q1=makeQuery(id+"F34.opExtrude","CAP_EDGE",EDGE,{"disambiguationData":[OSD([sQuery(id+"F32.wireOp",EDGE,"E147")])],"isStart":false});
            var Q2;
            Q2=makeQuery(id+"F33.opExtrude","CAP_EDGE",EDGE,{"disambiguationData":[OSD([sQuery(id+"F32.wireOp",EDGE,"E148")])],"isStart":false});
            var Q3;
            Q3=makeQuery(id+"F34.opExtrude","CAP_EDGE",EDGE,{"disambiguationData":[OSD([sQuery(id+"F32.wireOp",EDGE,"E148")])],"isStart":false});
            fillet(context, id + "F35", {"entities" : qUnion([Q0, Q1, Q2, Q3]), "radius" : .7 * mm, "tangentPropagation" : true, "allowEdgeOverflow" : false});
        }
        {
            var Q0;
            Q0=makeQuery(id+"F31.opExtrude","CAP_EDGE",EDGE,{"disambiguationData":[OSD([sQuery(id+"F28.wireOp",EDGE,"E123.bottom")])],"isStart":false});
            var Q1;
            Q1=makeQuery(id+"F31.opExtrude","CAP_EDGE",EDGE,{"disambiguationData":[OSD([sQuery(id+"F28.wireOp",EDGE,"E123.bottom")])],"isStart":true});
            var Q2;
            Q2=makeQuery(id+"F31.opExtrude","CAP_EDGE",EDGE,{"disambiguationData":[OSD([sQuery(id+"F28.wireOp",EDGE,"E127.trimOffspring")])],"isStart":false});
            var Q3;
            Q3=makeQuery(id+"F31.opExtrude","CAP_EDGE",EDGE,{"disambiguationData":[OSD([sQuery(id+"F28.wireOp",EDGE,"E127.trimOffspring")])],"isStart":true});
            var Q4;
            Q4=makeQuery(id+"F31.opExtrude","CAP_EDGE",EDGE,{"disambiguationData":[OSD([sQuery(id+"F28.wireOp",EDGE,"E123.top")])],"isStart":false});
            var Q5;
            Q5=makeQuery(id+"F31.opExtrude","CAP_EDGE",EDGE,{"disambiguationData":[OSD([sQuery(id+"F28.wireOp",EDGE,"E140.trimOffspring")])],"isStart":false});
            fillet(context, id + "F36", {"entities" : qUnion([Q0, Q1, Q2, Q3, Q4, Q5]), "radius" : 1 * mm, "tangentPropagation" : true, "allowEdgeOverflow" : false});
        }
        {
            var Q0;
            Q0=makeQuery(id+"F31.opExtrude","SWEPT_FACE",FACE,{"disambiguationData":[OSD([sQuery(id+"F28.wireOp",EDGE,"E125")])]});
            var sketch = newSketch(context, id + "F37", { "sketchPlane" : qUnion([Q0])});
            skLineSegment(sketch, "E149.bottom", {"start": v(3.5, 0) * mm, "end": v(16.5, 0) * mm});
            skLineSegment(sketch, "E149.top", {"start": v(5.5, 4) * mm, "end": v(14.5, 4) * mm});
            skLineSegment(sketch, "E149.left", {"start": v(3.5, 0) * mm, "end": v(3.5, 2) * mm});
            skLineSegment(sketch, "E149.right", {"start": v(16.5, 0) * mm, "end": v(16.5, 2) * mm});
            skLineSegment(sketch, "E150.bottom", {"start": v(5.5, 1) * mm, "end": v(14.5, 1) * mm});
            skLineSegment(sketch, "E150.top", {"start": v(5.5, 3) * mm, "end": v(14.5, 3) * mm});
            skLineSegment(sketch, "E150.left", {"start": v(4.5, 2) * mm, "end": v(4.5, 2) * mm});
            skLineSegment(sketch, "E150.right", {"start": v(15.5, 2) * mm, "end": v(15.5, 2) * mm});
            skPoint(sketch, "E151.visualSharp", {"position": v(4.5, 3) * mm});
            skArc(sketch, "E151.filletArc", {"start": v(5.5, 3) * mm, "mid": v(4.8, 2.7) * mm, "end": v(4.5, 2) * mm});
            skPoint(sketch, "E152.visualSharp", {"position": v(4.5, 1) * mm});
            skArc(sketch, "E152.filletArc", {"start": v(4.5, 2) * mm, "mid": v(4.8, 1.3) * mm, "end": v(5.5, 1) * mm});
            skPoint(sketch, "E153.visualSharp", {"position": v(15.5, 1) * mm});
            skArc(sketch, "E153.filletArc", {"start": v(14.5, 1) * mm, "mid": v(15.2, 1.3) * mm, "end": v(15.5, 2) * mm});
            skPoint(sketch, "E154.visualSharp", {"position": v(15.5, 3) * mm});
            skArc(sketch, "E154.filletArc", {"start": v(15.5, 2) * mm, "mid": v(15.2, 2.7) * mm, "end": v(14.5, 3) * mm});
            skPoint(sketch, "E155.visualSharp", {"position": v(3.5, 4) * mm});
            skArc(sketch, "E155.filletArc", {"start": v(5.5, 4) * mm, "mid": v(4.09, 3.41) * mm, "end": v(3.5, 2) * mm});
            skPoint(sketch, "E156.visualSharp", {"position": v(16.5, 4) * mm});
            skArc(sketch, "E156.filletArc", {"start": v(16.5, 2) * mm, "mid": v(15.91, 3.41) * mm, "end": v(14.5, 4) * mm});
            skSolve(sketch);
        }
        {
            var Q0;
            Q0=makeQuery(id+"F37.imprint","IMPRINT",FACE,{"disambiguationData":[TD([[makeQuery(id+"F37.imprint","IMPRINT",EDGE,{"derivedFrom":sQuery(id+"F37.wireOp",EDGE,"E149.top")}),-1.0]])]});
            var Q1;
            Q1=makeQuery(id+"F37.imprint","IMPRINT",FACE,{"disambiguationData":[TD([[makeQuery(id+"F37.imprint","IMPRINT",EDGE,{"derivedFrom":sQuery(id+"F37.wireOp",EDGE,"E150.top")}),-1.0]])]});
            var Q2;
            Q2=makeQuery(id+"F31.opExtrude","SWEPT_FACE",FACE,{"disambiguationData":[OSD([sQuery(id+"F28.wireOp",EDGE,"E123.top")])]});
            extrude(context, id + "F38", {"entities" : qUnion([Q0, Q1]), "operationType" : NewBodyOperationType.ADD, "endBound" : BoundingType.UP_TO_SURFACE, "oppositeDirection" : true, "depth" : 3 * mm, "endBoundEntityFace" : qUnion([Q2]), "offsetDistance" : 25 * mm});
        }
        {
            var Q0;
            Q0=makeQuery(id+"F37.imprint","IMPRINT",FACE,{"disambiguationData":[TD([[makeQuery(id+"F37.imprint","IMPRINT",EDGE,{"derivedFrom":sQuery(id+"F37.wireOp",EDGE,"E150.bottom")}),1.0]])]});
            var Q1;
            Q1=makeQuery(id+"F37.imprint","IMPRINT",FACE,{"disambiguationData":[TD([[makeQuery(id+"F37.imprint","IMPRINT",EDGE,{"derivedFrom":sQuery(id+"F37.wireOp",EDGE,"E150.top")}),-1.0]])]});
            extrude(context, id + "F39", {"entities" : qUnion([Q0, Q1]), "operationType" : NewBodyOperationType.REMOVE, "oppositeDirection" : true, "depth" : 25 * mm, "offsetDistance" : 25 * mm});
        }
        {
            var Q0;
            Q0=makeQuery(id+"F30.imprint","IMPRINT",FACE,{"disambiguationData":[TD([[makeQuery(id+"F30.imprint","IMPRINT",EDGE,{"derivedFrom":sQuery(id+"F30.wireOp",EDGE,"E146")}),1.0]])]});
            extrude(context, id + "F40", {"entities" : qUnion([Q0]), "endBound" : BoundingType.SYMMETRIC, "depth" : 21.5 * mm, "offsetDistance" : 25 * mm});
        }
        {
            var Q0;
            Q0=makeQuery(id+"F40.opExtrude","CAP_EDGE",EDGE,{"disambiguationData":[OSD([sQuery(id+"F30.wireOp",EDGE,"E146")])],"isStart":true});
            var Q1;
            Q1=makeQuery(id+"F40.opExtrude","CAP_EDGE",EDGE,{"disambiguationData":[OSD([sQuery(id+"F30.wireOp",EDGE,"E146")])],"isStart":false});
            fillet(context, id + "F41", {"entities" : qUnion([Q0, Q1]), "radius" : .75 * mm, "tangentPropagation" : true, "allowEdgeOverflow" : false});
        }
        {
            var Q0;
            Q0=makeQuery(id+"F40.opExtrude","SWEPT_BODY",BODY,{"disambiguationData":[OSD([sQuery(id+"F30.wireOp",EDGE,"E146")])]});
            var Q1;
            Q1=makeQuery(id+"F13.opExtrude","SWEPT_BODY",BODY,{"disambiguationData":[OSD([sQuery(id+"F12.wireOp",EDGE,"E74.bottom"),sQuery(id+"F12.wireOp",EDGE,"E74.top"),sQuery(id+"F12.wireOp",EDGE,"E74.left"),sQuery(id+"F12.wireOp",EDGE,"E74.right"),sQuery(id+"F12.wireOp",EDGE,"E75.filletArc"),sQuery(id+"F12.wireOp",EDGE,"E76.filletArc"),sQuery(id+"F12.wireOp",EDGE,"E77.filletArc"),sQuery(id+"F12.wireOp",EDGE,"E78.filletArc")])]});
            booleanBodies(context, id + "F42", {"operationType" : BooleanOperationType.SUBTRACTION, "tools" : qUnion([Q0]), "targets" : qUnion([Q1])});
        }
        {
            var Q0;
            Q0=makeQuery(id+"F13.opExtrude","SWEPT_BODY",BODY,{"disambiguationData":[OSD([sQuery(id+"F12.wireOp",EDGE,"E74.bottom"),sQuery(id+"F12.wireOp",EDGE,"E74.top"),sQuery(id+"F12.wireOp",EDGE,"E74.left"),sQuery(id+"F12.wireOp",EDGE,"E74.right"),sQuery(id+"F12.wireOp",EDGE,"E75.filletArc"),sQuery(id+"F12.wireOp",EDGE,"E76.filletArc"),sQuery(id+"F12.wireOp",EDGE,"E77.filletArc"),sQuery(id+"F12.wireOp",EDGE,"E78.filletArc")])]});
            var Q1;
            Q1=qCreatedBy(makeId("Right.planeOp"),FACE);
            mirror(context, id + "F43", {"entities" : qUnion([Q0]), "mirrorPlane" : qUnion([Q1])});
        }
    });
